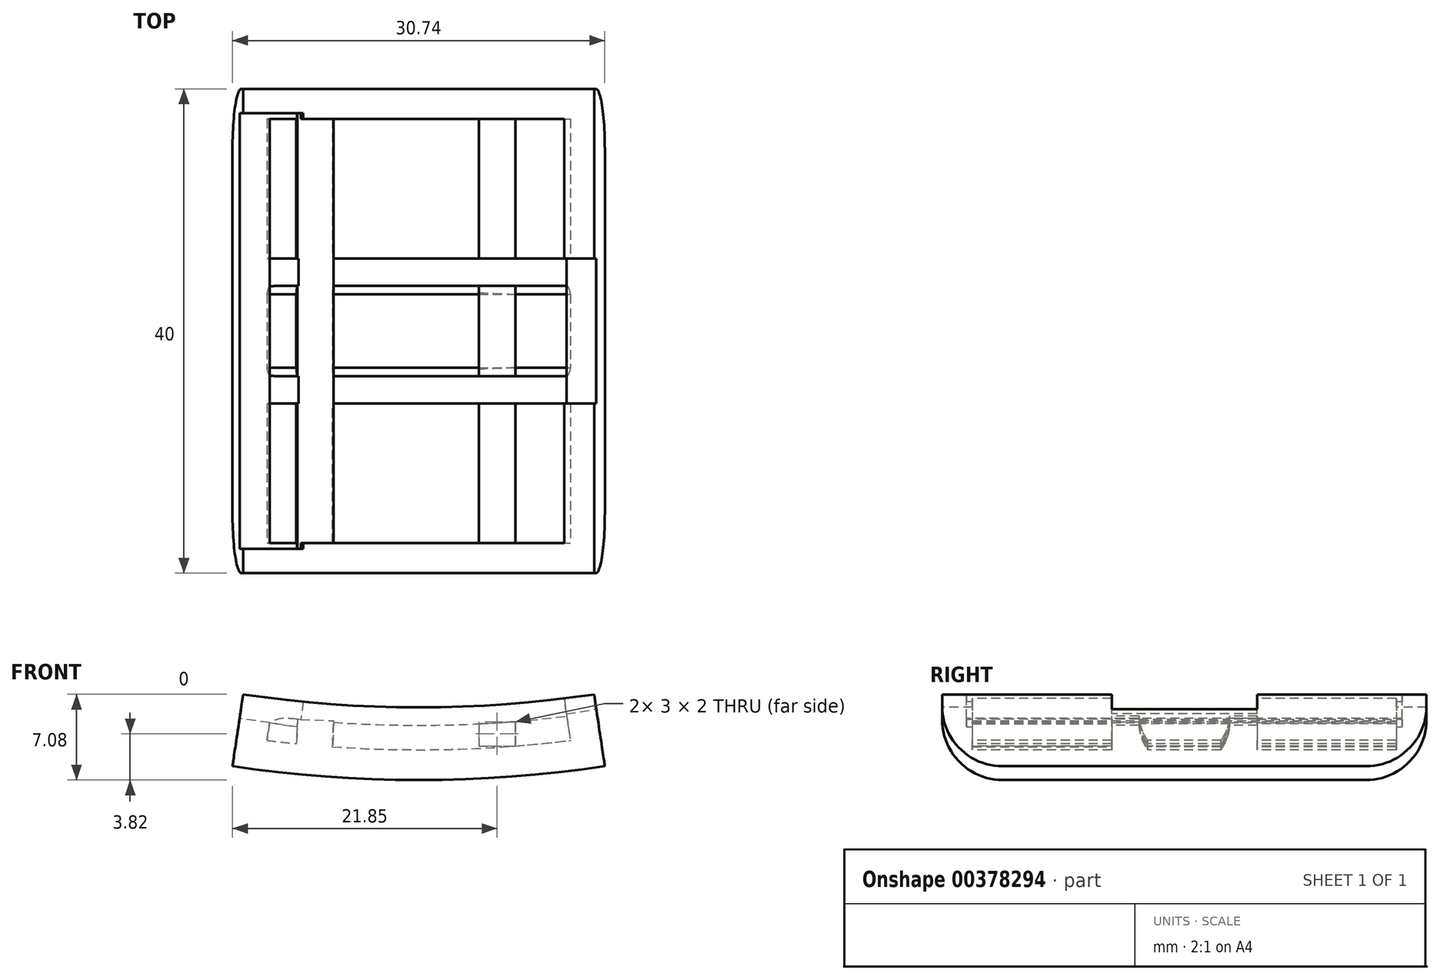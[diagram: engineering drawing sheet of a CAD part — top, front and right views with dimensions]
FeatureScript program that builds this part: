
annotation { "Feature Type Name" : "Feature", "Feature Type Description" : "" }
export const myFeature = defineFeature(function(context is Context, id is Id, definition is map)
    precondition{}
    {
        {
            var Q0;
            Q0=qCreatedBy(makeId("Right.planeOp"),FACE);
            var sketch = newSketch(context, id + "F0", { "sketchPlane" : qUnion([Q0])});
            skLineSegment(sketch, "E0.bottom", {"start": v(-31.09, -16.82) * mm, "end": v(8.91, -16.82) * mm});
            skLineSegment(sketch, "E0.top", {"start": v(-31.09, -16.32) * mm, "end": v(8.91, -16.32) * mm});
            skLineSegment(sketch, "E0.left", {"start": v(-31.09, -16.82) * mm, "end": v(-31.09, -16.32) * mm});
            skLineSegment(sketch, "E0.right", {"start": v(8.91, -16.82) * mm, "end": v(8.91, -16.32) * mm});
            skPoint(sketch, "E0.middle", {"position": v(-11.09, -8.82) * mm});
            skFitSpline(sketch, "E1", {"points": [v(-31.09, -16.32) * mm, v(-11.09, -8.82) * mm, v(8.91, -16.32) * mm], "startDerivative": vector(5.73, 40.41) * mm, "endDerivative": vector(9.08, -43.36) * mm});
            skLineSegment(sketch, "E2", {"start": v(-11.09, -8.82) * mm, "end": v(-11.09, 81.18) * mm});
            skPoint(sketch, "E3", {"position": v(-11.09, 81.18) * mm});
            skLineSegment(sketch, "E4", {"start": v(-77.22, 81.18) * mm, "end": v(56.91, 81.18) * mm});
            skLineSegment(sketch, "E5.top", {"start": v(-31.09, -22.82) * mm, "end": v(8.91, -22.82) * mm});
            skLineSegment(sketch, "E5.left", {"start": v(-31.09, -16.82) * mm, "end": v(-31.09, -22.82) * mm});
            skLineSegment(sketch, "E5.right", {"start": v(8.91, -16.82) * mm, "end": v(8.91, -22.82) * mm});
            skSolve(sketch);
        }
        {
            var Q0;
            Q0=makeQuery(id+"F0.imprint","IMPRINT",FACE,{"disambiguationData":[TD([[makeQuery(id+"F0.imprint","IMPRINT",EDGE,{"derivedFrom":sQuery(id+"F0.wireOp",EDGE,"E0.bottom")}),-1.0]])]});
            var Q1;
            Q1=sQuery(id+"F0.wireOp",EDGE,"E4");
            revolve(context, id + "F1", {"entities" : qUnion([Q0]), "axis" : qUnion([Q1]), "revolveType" : RevolveType.SYMMETRIC, "angle" : 17 * degree});
        }
        {
            var Q0;
            Q0=makeQuery(id+"F1.opRevolve","SWEPT_FACE",FACE,{"disambiguationData":[OSD([sQuery(id+"F0.wireOp",EDGE,"E0.bottom")])]});
            shell(context, id + "F2", {"entities" : qUnion([Q0]), "thickness" : 2.5 * mm});
        }
        {
            var Q0;
            Q0=makeQuery(id+"F1.opRevolve","SWEPT_EDGE",EDGE,{"disambiguationData":[OSD([sQuery(id+"F0.wireOp",EDGE,"E5.top"),sQuery(id+"F0.wireOp",EDGE,"E5.right")])]});
            var Q1;
            Q1=makeQuery(id+"F1.opRevolve","SWEPT_EDGE",EDGE,{"disambiguationData":[OSD([sQuery(id+"F0.wireOp",EDGE,"E5.top"),sQuery(id+"F0.wireOp",EDGE,"E5.left")])]});
            fillet(context, id + "F3", {"entities" : qUnion([Q0, Q1]), "radius" : 5 * mm, "tangentPropagation" : true, "allowEdgeOverflow" : false});
        }
        {
            var Q0;
            Q0=makeQuery(id+"F1.opRevolve","CAP_FACE",FACE,{"disambiguationData":[OSD([sQuery(id+"F0.wireOp",EDGE,"E0.bottom"),sQuery(id+"F0.wireOp",EDGE,"E5.top"),sQuery(id+"F0.wireOp",EDGE,"E5.left"),sQuery(id+"F0.wireOp",EDGE,"E5.right")])],"isStart":true});
            var sketch = newSketch(context, id + "F4", { "sketchPlane" : qUnion([Q0])});
            skLineSegment(sketch, "E6.bottom", {"start": v(-5.09, -18.96) * mm, "end": v(-17.09, -18.96) * mm});
            skLineSegment(sketch, "E6.top", {"start": v(-5.09, -16.46) * mm, "end": v(-17.09, -16.46) * mm});
            skLineSegment(sketch, "E6.left", {"start": v(-5.09, -18.96) * mm, "end": v(-5.09, -16.46) * mm});
            skLineSegment(sketch, "E6.right", {"start": v(-17.09, -18.96) * mm, "end": v(-17.09, -16.46) * mm});
            skPoint(sketch, "E6.middle", {"position": v(-11.09, -17.71) * mm});
            skSolve(sketch);
        }
        {
            var Q0;
            {var subQ0=sQuery(id+"F4.wireOp",EDGE,"E6.bottom");Q0=makeQuery(id+"F4.imprint","IMPRINT",FACE,{"disambiguationData":[TD([[makeQuery(id+"F4.imprint","IMPRINT",EDGE,{"derivedFrom":subQ0}),-1.0]])]});}
            var Q1;
            {var subQ0=sQuery(id+"F4.wireOp",EDGE,"E6.top");Q1=makeQuery(id+"F4.imprint","IMPRINT",FACE,{"disambiguationData":[TD([[makeQuery(id+"F4.imprint","IMPRINT",EDGE,{"derivedFrom":subQ0}),1.0]])]});}
            extrude(context, id + "F5", {"entities" : qUnion([Q0, Q1]), "operationType" : NewBodyOperationType.REMOVE, "oppositeDirection" : true, "depth" : 5 * mm, "offsetDistance" : 25 * mm});
        }
        {
            var Q0;
            Q0=makeQuery(id+"F1.opRevolve","CAP_FACE",FACE,{"disambiguationData":[OSD([sQuery(id+"F0.wireOp",EDGE,"E0.bottom"),sQuery(id+"F0.wireOp",EDGE,"E5.top"),sQuery(id+"F0.wireOp",EDGE,"E5.left"),sQuery(id+"F0.wireOp",EDGE,"E5.right")])],"isStart":false});
            var sketch = newSketch(context, id + "F6", { "sketchPlane" : qUnion([Q0])});
            skPoint(sketch, "E7", {"position": v(11.09, -17.71) * mm});
            skLineSegment(sketch, "E8.bottom", {"start": v(-6.91, -19.71) * mm, "end": v(29.09, -19.71) * mm});
            skLineSegment(sketch, "E8.top", {"start": v(-6.91, -15.71) * mm, "end": v(29.09, -15.71) * mm});
            skLineSegment(sketch, "E8.left", {"start": v(-6.91, -19.71) * mm, "end": v(-6.91, -15.71) * mm});
            skLineSegment(sketch, "E8.right", {"start": v(29.09, -19.71) * mm, "end": v(29.09, -15.71) * mm});
            skSolve(sketch);
        }
        {
            var Q0;
            Q0 = qSketchRegion(id + "F6", true);
            extrude(context, id + "F7", {"entities" : qUnion([Q0]), "operationType" : NewBodyOperationType.REMOVE, "oppositeDirection" : true, "depth" : 5 * mm, "offsetDistance" : 25 * mm});
        }
        {
            var Q0;
            {var subQ0=sQuery(id+"F0.wireOp",EDGE,"E5.right");var subQ1=sQuery(id+"F0.wireOp",EDGE,"E5.left");var subQ2=sQuery(id+"F0.wireOp",EDGE,"E5.top");var subQ3=sQuery(id+"F0.wireOp",EDGE,"E0.bottom");Q0=makeQuery(id+"F2.opShell","OFFSET_FACE",FACE,{"disambiguationData":[OSD([subQ3,subQ2,subQ1,subQ0]),TDD([makeQuery(id+"F1.opRevolve","CAP_FACE",FACE,{"disambiguationData":[OSD([subQ3,subQ2,subQ1,subQ0])],"isStart":true})])]});}
            var sketch = newSketch(context, id + "F8", { "sketchPlane" : qUnion([Q0])});
            skCircle(sketch, "E9", {"center": v(11.09, -18.96) * mm, "radius": 3.5 * mm, "construction": true});
            skPoint(sketch, "E10", {"position": v(14.59, -18.96) * mm});
            skPoint(sketch, "E11", {"position": v(7.59, -18.96) * mm});
            skPoint(sketch, "E12", {"position": v(17.09, -18.96) * mm});
            skPoint(sketch, "E13", {"position": v(5.09, -18.96) * mm});
            skLineSegment(sketch, "E14", {"start": v(5.09, -18.96) * mm, "end": v(5.09, -21.18) * mm, "construction": true});
            skLineSegment(sketch, "E15", {"start": v(17.09, -18.96) * mm, "end": v(17.09, -21.18) * mm, "construction": true});
            skLineSegment(sketch, "E16", {"start": v(5.09, -18.96) * mm, "end": v(7.59, -18.96) * mm});
            skLineSegment(sketch, "E17", {"start": v(5.09, -18.96) * mm, "end": v(5.09, -21.18) * mm});
            skLineSegment(sketch, "E18", {"start": v(5.09, -21.18) * mm, "end": v(17.09, -21.18) * mm});
            skLineSegment(sketch, "E19", {"start": v(17.09, -21.18) * mm, "end": v(17.09, -18.96) * mm});
            skLineSegment(sketch, "E20", {"start": v(17.09, -18.96) * mm, "end": v(14.59, -18.96) * mm});
            skCircle(sketch, "E21", {"center": v(11.09, -18.96) * mm, "radius": 3.75 * mm});
            skLineSegment(sketch, "E22", {"start": v(5.09, -19.16) * mm, "end": v(17.09, -19.16) * mm});
            skSolve(sketch);
        }
        {
            var Q0;
            {var subQ0=sQuery(id+"F8.wireOp",EDGE,"E22");var subQ6=sQuery(id+"F8.wireOp",EDGE,"E21");var subQ7=makeQuery(id+"F8.imprint","INTERSECT",VERTEX,{"disambiguationData":[OD(0.0)],"derivedFrom":[subQ6,subQ0]});Q0=makeQuery(id+"F8.imprint","IMPRINT",FACE,{"disambiguationData":[TD([[makeQuery(id+"F8.imprint","IMPRINT",EDGE,{"disambiguationData":[TD([[subQ7,-1.0]])],"derivedFrom":subQ6}),-1.0]])]});}
            var Q1;
            {var subQ1=sQuery(id+"F8.wireOp",EDGE,"E18");var subQ4=sQuery(id+"F8.wireOp",EDGE,"E21");var subQ5=makeQuery(id+"F8.imprint","INTERSECT",VERTEX,{"disambiguationData":[OD(1.0)],"derivedFrom":[subQ1,subQ4]});Q1=makeQuery(id+"F8.imprint","IMPRINT",FACE,{"disambiguationData":[TD([[makeQuery(id+"F8.imprint","IMPRINT",EDGE,{"disambiguationData":[TD([[subQ5,-1.0]])],"derivedFrom":subQ4}),-1.0]])]});}
            var Q2;
            Q2=sQuery(id+"F0.wireOp",EDGE,"E4");
            revolve(context, id + "F9", {"operationType" : NewBodyOperationType.ADD, "surfaceOperationType" : NewSurfaceOperationType.NEW, "entities" : qUnion([Q0, Q1]), "axis" : qUnion([Q2]), "revolveType" : RevolveType.ONE_DIRECTION, "angle" : 14.5 * degree});
        }
        {
            var Q0;
            {var subQ0=sQuery(id+"F8.wireOp",EDGE,"E22");Q0=makeQuery(id+"F9.opRevolve","CAP_EDGE",EDGE,{"disambiguationData":[OSD([subQ0]),TDD([makeQuery(id+"F8.imprint","IMPRINT",EDGE,{"disambiguationData":[TD([[makeQuery(id+"F8.imprint","INTERSECT",VERTEX,{"derivedFrom":[sQuery(id+"F8.wireOp",EDGE,"E17"),subQ0]}),-1.0]])],"derivedFrom":subQ0})])],"isStart":false});}
            var Q1;
            {var subQ0=sQuery(id+"F8.wireOp",EDGE,"E22");Q1=makeQuery(id+"F9.opRevolve","CAP_EDGE",EDGE,{"disambiguationData":[OSD([subQ0]),TDD([makeQuery(id+"F8.imprint","IMPRINT",EDGE,{"disambiguationData":[TD([[makeQuery(id+"F8.imprint","INTERSECT",VERTEX,{"derivedFrom":[sQuery(id+"F8.wireOp",EDGE,"E19"),subQ0]}),1.0]])],"derivedFrom":subQ0})])],"isStart":false});}
            fillet(context, id + "F10", {"entities" : qUnion([Q0, Q1]), "tangentPropagation" : true, "crossSection" : FilletCrossSection.CURVATURE, "radius" : 2.9 * mm, "magnitude" : 0.6, "defaultsChanged" : true, "isVariable" : true, "vertexSettings" : [], "smoothTransition" : false});
        }
        {
            var Q0;
            Q0=makeQuery(id+"F9.opRevolve","SWEPT_FACE",FACE,{"disambiguationData":[OSD([sQuery(id+"F8.wireOp",EDGE,"E19")])]});
            var sketch = newSketch(context, id + "F11", { "sketchPlane" : qUnion([Q0])});
            skPoint(sketch, "E23", {"position": v(1.11, -18.3) * mm});
            skLineSegment(sketch, "E24", {"start": v(1.11, -18.3) * mm, "end": v(-10.01, -17.8) * mm, "construction": true});
            skLineSegment(sketch, "E25.bottom", {"start": v(-10.01, -17.8) * mm, "end": v(-7.02, -17.93) * mm});
            skLineSegment(sketch, "E25.top", {"start": v(-10.1, -19.94) * mm, "end": v(-7.11, -20.07) * mm});
            skLineSegment(sketch, "E25.left", {"start": v(-10.01, -17.8) * mm, "end": v(-10.1, -19.94) * mm});
            skLineSegment(sketch, "E25.right", {"start": v(-7.02, -17.93) * mm, "end": v(-7.11, -20.07) * mm});
            skLineSegment(sketch, "E26", {"start": v(-7.02, -17.93) * mm, "end": v(4.98, -18.18) * mm});
            skLineSegment(sketch, "E27.bottom", {"start": v(4.98, -18.18) * mm, "end": v(7.98, -18) * mm});
            skLineSegment(sketch, "E27.top", {"start": v(4.98, -20) * mm, "end": v(7.98, -20) * mm});
            skLineSegment(sketch, "E27.left", {"start": v(4.98, -18.18) * mm, "end": v(4.98, -20) * mm});
            skLineSegment(sketch, "E27.right", {"start": v(7.98, -18) * mm, "end": v(7.98, -20) * mm});
            skSolve(sketch);
        }
        {
            var Q0;
            Q0 = qSketchRegion(id + "F11", true);
            extrude(context, id + "F12", {"entities" : qUnion([Q0]), "operationType" : NewBodyOperationType.ADD, "endBound" : BoundingType.UP_TO_NEXT, "depth" : 25 * mm, "offsetDistance" : 25 * mm});
        }
        {
            var Q0;
            Q0 = qSketchRegion(id + "F11", true);
            extrude(context, id + "F13", {"entities" : qUnion([Q0]), "operationType" : NewBodyOperationType.ADD, "oppositeDirection" : true, "depth" : 25 * mm, "offsetDistance" : 25 * mm});
        }
    });
